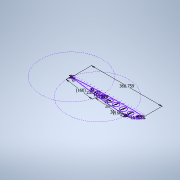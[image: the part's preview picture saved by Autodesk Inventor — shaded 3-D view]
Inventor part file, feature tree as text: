
AUTODESK INVENTOR PART (.ipt)
format: ipt  version: 2021 (Build 250183000, 183)  size: 154,112 bytes
history: native  units: mm
features: sketch x1
ambient origin geometry x8: Origin, YZ Plane, XZ Plane, XY Plane, X Axis, Y Axis, Z Axis, Center Point
feature tree (1):
  sketch  "Sketch1"  dims[d5=160.0mm d8=160.0mm d17=5.0mm d18=5.0mm d25=6.0mm d26=5.0mm d27=5.0mm d30=17.227785mm d31=34.456mm d36=5.0mm d37=5.0mm d41=23.0mm d50=368.759386mm d51=15.0mm d52=28.0mm d53=30.0mm d54=25.0mm d57=15.0mm d58=15.0mm d59=25.0mm d60=8.0mm d61=23.0mm]
